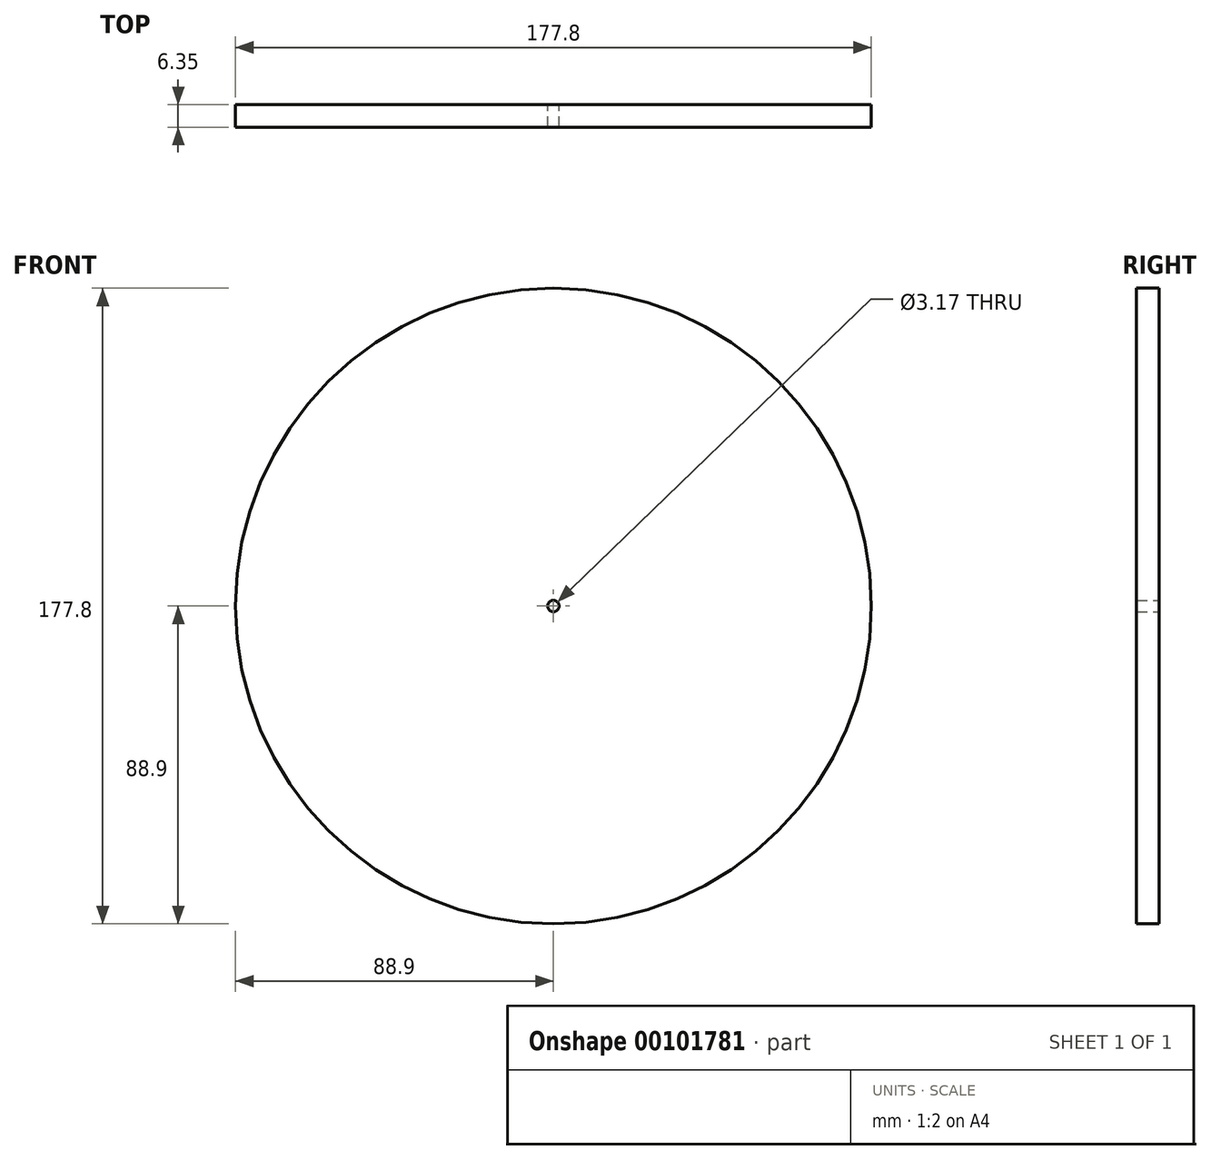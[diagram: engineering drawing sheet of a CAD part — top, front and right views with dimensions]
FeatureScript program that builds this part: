
annotation { "Feature Type Name" : "Feature", "Feature Type Description" : "" }
export const myFeature = defineFeature(function(context is Context, id is Id, definition is map)
    precondition{}
    {
        {
            var Q0;
            Q0=qCreatedBy(makeId("Front.planeOp"),FACE);
            var sketch = newSketch(context, id + "F0", { "sketchPlane" : qUnion([Q0])});
            skCircle(sketch, "E0", {"center": v(0, 0) * mm, "radius": 88.9 * mm});
            skCircle(sketch, "E1", {"center": v(0, 0) * mm, "radius": 1.59 * mm});
            skSolve(sketch);
        }
        {
            var Q0;
            Q0=makeQuery(id+"F0.imprint","IMPRINT",FACE,{"disambiguationData":[TD([[makeQuery(id+"F0.imprint","IMPRINT",EDGE,{"derivedFrom":sQuery(id+"F0.wireOp",EDGE,"E0")}),1.0]])]});
            extrude(context, id + "F1", {"entities" : qUnion([Q0]), "depth" : 6.35 * mm});
        }
    });
